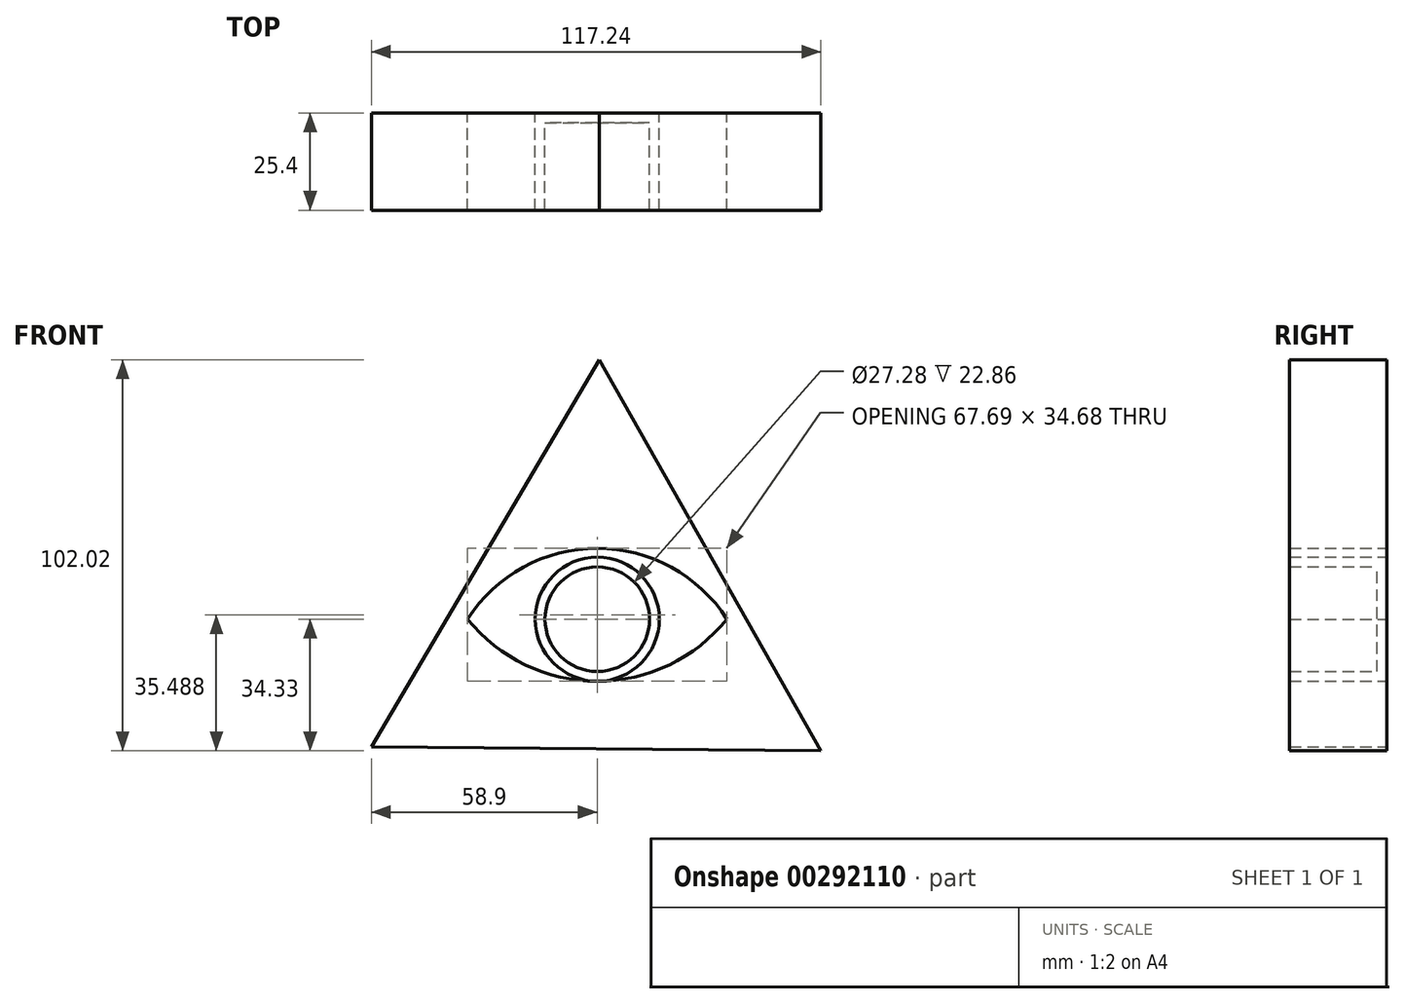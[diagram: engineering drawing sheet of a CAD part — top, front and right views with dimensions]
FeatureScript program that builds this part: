
annotation { "Feature Type Name" : "Feature", "Feature Type Description" : "" }
export const myFeature = defineFeature(function(context is Context, id is Id, definition is map)
    precondition{}
    {
        {
            var Q0;
            Q0=qCreatedBy(makeId("Front.planeOp"),FACE);
            var sketch = newSketch(context, id + "F0", { "sketchPlane" : qUnion([Q0])});
            skCircle(sketch, "E0.cCircle", {"center": v(0, 0) * mm, "radius": 33.85 * mm, "construction": true});
            skLineSegment(sketch, "E0.0", {"start": v(0.56, 67.69) * mm, "end": v(58.34, -34.33) * mm});
            skLineSegment(sketch, "E0.1", {"start": v(58.34, -34.33) * mm, "end": v(-58.9, -33.36) * mm});
            skLineSegment(sketch, "E0.2", {"start": v(-58.9, -33.36) * mm, "end": v(0.56, 67.69) * mm});
            skPoint(sketch, "E0.0.midPoint", {"position": v(29.45, 16.68) * mm});
            skArc(sketch, "E1", {"start": v(33.85, 0) * mm, "mid": v(0, 18.5) * mm, "end": v(-33.85, 0) * mm});
            skArc(sketch, "E2", {"start": v(-33.85, 0) * mm, "mid": v(0, -16.18) * mm, "end": v(33.85, 0) * mm});
            skCircle(sketch, "E3", {"center": v(0, 0) * mm, "radius": 16.18 * mm});
            skSolve(sketch);
        }
        {
            var Q0;
            Q0 = qSketchRegion(id + "F0", true);
            var Q1;
            Q1=makeQuery(id+"F0.imprint","IMPRINT",FACE,{"disambiguationData":[TD([[makeQuery(id+"F0.imprint","IMPRINT",EDGE,{"derivedFrom":sQuery(id+"F0.wireOp",EDGE,"E3")}),1.0]])]});
            extrude(context, id + "F1", {"entities" : qUnion([Q0, Q1]), "depth" : 25.4 * mm});
        }
        {
            var Q0;
            Q0=makeQuery(id+"F1.opExtrude","CAP_FACE",FACE,{"disambiguationData":[OSD([sQuery(id+"F0.wireOp",EDGE,"E3")])],"isStart":false});
            shell(context, id + "F2", {"entities" : qUnion([Q0]), "thickness" : 2.54 * mm});
        }
    });
